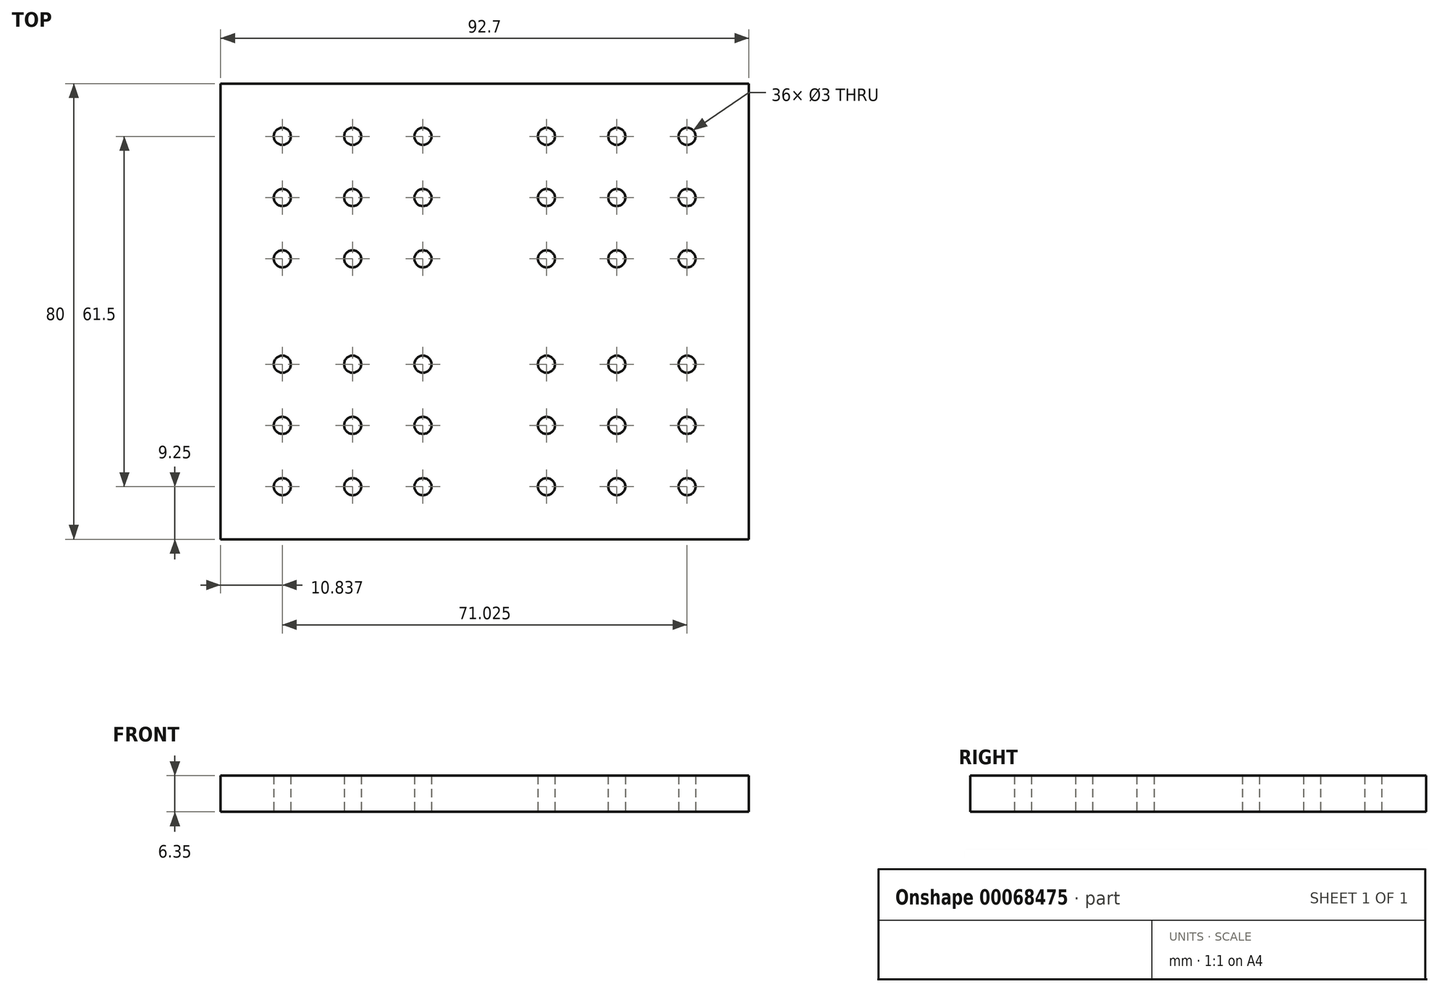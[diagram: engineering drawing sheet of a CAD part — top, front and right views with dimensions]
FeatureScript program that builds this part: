
annotation { "Feature Type Name" : "Feature", "Feature Type Description" : "" }
export const myFeature = defineFeature(function(context is Context, id is Id, definition is map)
    precondition{}
    {
        {
            var Q0;
            Q0=qCreatedBy(makeId("Top.planeOp"),FACE);
            var sketch = newSketch(context, id + "F0", { "sketchPlane" : qUnion([Q0])});
            skLineSegment(sketch, "E0.bottom", {"start": v(0, 0) * mm, "end": v(46.35, 0) * mm, "construction": true});
            skLineSegment(sketch, "E0.top", {"start": v(0, 40) * mm, "end": v(46.35, 40) * mm});
            skLineSegment(sketch, "E0.left", {"start": v(0, 0) * mm, "end": v(0, 40) * mm});
            skLineSegment(sketch, "E0.right", {"start": v(46.35, 0) * mm, "end": v(46.35, 40) * mm});
            skCircle(sketch, "E1", {"center": v(10.84, 30.75) * mm, "radius": 1.5 * mm});
            skCircle(sketch, "E2", {"center": v(23.17, 30.75) * mm, "radius": 1.5 * mm});
            skCircle(sketch, "E3", {"center": v(35.51, 30.75) * mm, "radius": 1.5 * mm});
            skCircle(sketch, "E4", {"center": v(10.84, 20) * mm, "radius": 1.5 * mm});
            skCircle(sketch, "E5", {"center": v(23.17, 20) * mm, "radius": 1.5 * mm});
            skCircle(sketch, "E6", {"center": v(35.51, 20) * mm, "radius": 1.5 * mm});
            skCircle(sketch, "E7", {"center": v(10.84, 9.25) * mm, "radius": 1.5 * mm});
            skCircle(sketch, "E8", {"center": v(23.17, 9.25) * mm, "radius": 1.5 * mm});
            skCircle(sketch, "E9", {"center": v(35.51, 9.25) * mm, "radius": 1.5 * mm});
            skLineSegment(sketch, "E10", {"start": v(0, 30.75) * mm, "end": v(9.34, 30.75) * mm, "construction": true});
            skLineSegment(sketch, "E11", {"start": v(12.34, 30.75) * mm, "end": v(21.67, 30.75) * mm, "construction": true});
            skLineSegment(sketch, "E12.trimOffspring", {"start": v(24.68, 30.75) * mm, "end": v(34.01, 30.75) * mm, "construction": true});
            skLineSegment(sketch, "E13.trimOffspring", {"start": v(37.01, 30.75) * mm, "end": v(46.35, 30.75) * mm, "construction": true});
            skLineSegment(sketch, "E14", {"start": v(10.84, 40) * mm, "end": v(10.84, 32.25) * mm, "construction": true});
            skLineSegment(sketch, "E15.trimOffspring", {"start": v(10.84, 29.25) * mm, "end": v(10.84, 21.5) * mm, "construction": true});
            skLineSegment(sketch, "E16.trimOffspring", {"start": v(10.84, 18.5) * mm, "end": v(10.84, 10.75) * mm, "construction": true});
            skLineSegment(sketch, "E17.trimOffspring", {"start": v(10.84, 7.75) * mm, "end": v(10.84, 0) * mm, "construction": true});
            skCircle(sketch, "E18.MirrorC", {"center": v(-10.84, 30.75) * mm, "radius": 1.5 * mm});
            skCircle(sketch, "E19.MirrorC", {"center": v(-10.84, 9.25) * mm, "radius": 1.5 * mm});
            skCircle(sketch, "E20.MirrorC", {"center": v(-35.51, 30.75) * mm, "radius": 1.5 * mm});
            skCircle(sketch, "E21.MirrorC", {"center": v(-35.51, 9.25) * mm, "radius": 1.5 * mm});
            skCircle(sketch, "E22.MirrorC", {"center": v(-23.17, 9.25) * mm, "radius": 1.5 * mm});
            skCircle(sketch, "E23.MirrorC", {"center": v(-23.17, 30.75) * mm, "radius": 1.5 * mm});
            skCircle(sketch, "E24.MirrorC", {"center": v(-35.51, 20) * mm, "radius": 1.5 * mm});
            skCircle(sketch, "E25.MirrorC", {"center": v(-23.17, 20) * mm, "radius": 1.5 * mm});
            skCircle(sketch, "E26.MirrorC", {"center": v(-10.84, 20) * mm, "radius": 1.5 * mm});
            skLineSegment(sketch, "E27.MirrorCS", {"start": v(-46.35, 0) * mm, "end": v(-46.35, 40) * mm});
            skLineSegment(sketch, "E28.MirrorCS", {"start": v(0, 40) * mm, "end": v(-46.35, 40) * mm});
            skCircle(sketch, "E29.MirrorC", {"center": v(-10.84, -30.75) * mm, "radius": 1.5 * mm});
            skCircle(sketch, "E30.MirrorC", {"center": v(10.84, -30.75) * mm, "radius": 1.5 * mm});
            skCircle(sketch, "E31.MirrorC", {"center": v(35.51, -30.75) * mm, "radius": 1.5 * mm});
            skCircle(sketch, "E32.MirrorC", {"center": v(10.84, -20) * mm, "radius": 1.5 * mm});
            skCircle(sketch, "E33.MirrorC", {"center": v(10.84, -9.25) * mm, "radius": 1.5 * mm});
            skCircle(sketch, "E34.MirrorC", {"center": v(-10.84, -9.25) * mm, "radius": 1.5 * mm});
            skCircle(sketch, "E35.MirrorC", {"center": v(-35.51, -30.75) * mm, "radius": 1.5 * mm});
            skCircle(sketch, "E36.MirrorC", {"center": v(-10.84, -20) * mm, "radius": 1.5 * mm});
            skCircle(sketch, "E37.MirrorC", {"center": v(-23.17, -20) * mm, "radius": 1.5 * mm});
            skCircle(sketch, "E38.MirrorC", {"center": v(-23.17, -9.25) * mm, "radius": 1.5 * mm});
            skCircle(sketch, "E39.MirrorC", {"center": v(23.17, -30.75) * mm, "radius": 1.5 * mm});
            skCircle(sketch, "E40.MirrorC", {"center": v(23.17, -20) * mm, "radius": 1.5 * mm});
            skCircle(sketch, "E41.MirrorC", {"center": v(35.51, -20) * mm, "radius": 1.5 * mm});
            skCircle(sketch, "E42.MirrorC", {"center": v(35.51, -9.25) * mm, "radius": 1.5 * mm});
            skCircle(sketch, "E43.MirrorC", {"center": v(-35.51, -20) * mm, "radius": 1.5 * mm});
            skCircle(sketch, "E44.MirrorC", {"center": v(-35.51, -9.25) * mm, "radius": 1.5 * mm});
            skCircle(sketch, "E45.MirrorC", {"center": v(23.17, -9.25) * mm, "radius": 1.5 * mm});
            skCircle(sketch, "E46.MirrorC", {"center": v(-23.17, -30.75) * mm, "radius": 1.5 * mm});
            skLineSegment(sketch, "E47.MirrorCS", {"start": v(0, -40) * mm, "end": v(46.35, -40) * mm});
            skLineSegment(sketch, "E48.MirrorCS", {"start": v(0, 0) * mm, "end": v(0, -40) * mm});
            skLineSegment(sketch, "E49.MirrorCS", {"start": v(46.35, 0) * mm, "end": v(46.35, -40) * mm});
            skLineSegment(sketch, "E50.MirrorCS", {"start": v(0, -40) * mm, "end": v(-46.35, -40) * mm});
            skLineSegment(sketch, "E51.MirrorCS", {"start": v(-46.35, 0) * mm, "end": v(-46.35, -40) * mm});
            skPoint(sketch, "E52.MirrorCS.end.orphan", {"position": v(10.84, -10.75) * mm});
            skPoint(sketch, "E52.MirrorCS.start.orphan", {"position": v(10.84, -18.5) * mm});
            skPoint(sketch, "E53.MirrorCS.end.orphan", {"position": v(10.84, 0) * mm});
            skPoint(sketch, "E53.MirrorCS.start.orphan", {"position": v(10.84, -7.75) * mm});
            skPoint(sketch, "E54.MirrorCS.end.orphan", {"position": v(10.84, -21.5) * mm});
            skPoint(sketch, "E54.MirrorCS.start.orphan", {"position": v(10.84, -29.25) * mm});
            skPoint(sketch, "E55.MirrorCS.end.orphan", {"position": v(21.67, -30.75) * mm});
            skPoint(sketch, "E55.MirrorCS.start.orphan", {"position": v(12.34, -30.75) * mm});
            skPoint(sketch, "E56.MirrorCS.end.orphan", {"position": v(10.84, -32.25) * mm});
            skPoint(sketch, "E56.MirrorCS.start.orphan", {"position": v(10.84, -40) * mm});
            skPoint(sketch, "E57.MirrorCS.end.orphan", {"position": v(34.01, -30.75) * mm});
            skPoint(sketch, "E57.MirrorCS.start.orphan", {"position": v(24.68, -30.75) * mm});
            skPoint(sketch, "E58.MirrorCS.end.orphan", {"position": v(46.35, -30.75) * mm});
            skPoint(sketch, "E58.MirrorCS.start.orphan", {"position": v(37.01, -30.75) * mm});
            skPoint(sketch, "E59.MirrorCS.end.orphan", {"position": v(-9.34, -30.75) * mm});
            skPoint(sketch, "E59.MirrorCS.start.orphan", {"position": v(0, -30.75) * mm});
            skPoint(sketch, "E60.MirrorCS.end.orphan", {"position": v(9.34, -30.75) * mm});
            skPoint(sketch, "E61.MirrorCS.end.orphan", {"position": v(-10.84, -32.25) * mm});
            skPoint(sketch, "E61.MirrorCS.start.orphan", {"position": v(-10.84, -40) * mm});
            skPoint(sketch, "E62.MirrorCS.end.orphan", {"position": v(-21.67, -30.75) * mm});
            skPoint(sketch, "E62.MirrorCS.start.orphan", {"position": v(-12.34, -30.75) * mm});
            skPoint(sketch, "E63.MirrorCS.end.orphan", {"position": v(-34.01, -30.75) * mm});
            skPoint(sketch, "E63.MirrorCS.start.orphan", {"position": v(-24.68, -30.75) * mm});
            skPoint(sketch, "E64.MirrorCS.end.orphan", {"position": v(-46.35, -30.75) * mm});
            skPoint(sketch, "E64.MirrorCS.start.orphan", {"position": v(-37.01, -30.75) * mm});
            skPoint(sketch, "E65.MirrorCS.end.orphan", {"position": v(-10.84, -21.5) * mm});
            skPoint(sketch, "E65.MirrorCS.start.orphan", {"position": v(-10.84, -29.25) * mm});
            skPoint(sketch, "E66.MirrorCS.end.orphan", {"position": v(-10.84, -10.75) * mm});
            skPoint(sketch, "E66.MirrorCS.start.orphan", {"position": v(-10.84, -18.5) * mm});
            skPoint(sketch, "E67.MirrorCS.start.orphan", {"position": v(-10.84, -7.75) * mm});
            skPoint(sketch, "E68.MirrorCS.end.orphan", {"position": v(-10.84, 0) * mm});
            skPoint(sketch, "E68.MirrorCS.start.orphan", {"position": v(-10.84, 7.75) * mm});
            skPoint(sketch, "E69.MirrorCS.end.orphan", {"position": v(-10.84, 10.75) * mm});
            skPoint(sketch, "E69.MirrorCS.start.orphan", {"position": v(-10.84, 18.5) * mm});
            skPoint(sketch, "E70.MirrorCS.end.orphan", {"position": v(-10.84, 21.5) * mm});
            skPoint(sketch, "E70.MirrorCS.start.orphan", {"position": v(-10.84, 29.25) * mm});
            skPoint(sketch, "E71.MirrorCS.end.orphan", {"position": v(-9.34, 30.75) * mm});
            skPoint(sketch, "E71.MirrorCS.start.orphan", {"position": v(0, 30.75) * mm});
            skPoint(sketch, "E72.MirrorCS.end.orphan", {"position": v(-10.84, 32.25) * mm});
            skPoint(sketch, "E72.MirrorCS.start.orphan", {"position": v(-10.84, 40) * mm});
            skPoint(sketch, "E73.MirrorCS.end.orphan", {"position": v(-21.67, 30.75) * mm});
            skPoint(sketch, "E73.MirrorCS.start.orphan", {"position": v(-12.34, 30.75) * mm});
            skPoint(sketch, "E74.MirrorCS.end.orphan", {"position": v(-34.01, 30.75) * mm});
            skPoint(sketch, "E74.MirrorCS.start.orphan", {"position": v(-24.68, 30.75) * mm});
            skPoint(sketch, "E75.MirrorCS.end.orphan", {"position": v(-46.35, 30.75) * mm});
            skPoint(sketch, "E75.MirrorCS.start.orphan", {"position": v(-37.01, 30.75) * mm});
            skPoint(sketch, "E76.orphan", {"position": v(0, 0) * mm});
            skPoint(sketch, "E77.MirrorCS.end.orphan", {"position": v(-46.35, 0) * mm});
            skSolve(sketch);
        }
        {
            var Q0;
            Q0=makeQuery(id+"F0.imprint","IMPRINT",FACE,{"disambiguationData":[TD([[makeQuery(id+"F0.imprint","IMPRINT",EDGE,{"derivedFrom":sQuery(id+"F0.wireOp",EDGE,"E0.top")}),-1.0]])]});
            var Q1;
            Q1=makeQuery(id+"F0.imprint","IMPRINT",FACE,{"disambiguationData":[TD([[makeQuery(id+"F0.imprint","IMPRINT",EDGE,{"derivedFrom":sQuery(id+"F0.wireOp",EDGE,"E0.left")}),1.0]])]});
            extrude(context, id + "F1", {"entities" : qUnion([Q0, Q1]), "depth" : 6.35 * mm});
        }
    });
